# Revit family: oventrop_regudis-w-ht-duo_1341372rfa
name_source: partatom
category: Оборудование
revit_build: Autodesk Revit 2017 (Build: 20160225_1515(x64)
units: mm (PartAtom-declared; Revit-internal decimal feet)

## family parameters
Всегда вертикально = Да
Заголовок OmniClass = Climate Control (HVAC)
На основе рабочей плоскости = Нет
Номер OmniClass = 23.75.00.00
Общий = Нет
При загрузке вырезать с полостями = Нет
Размер круглого соединителя = Использовать диаметр
Тип детали = Нормальный
Точка расчета площади = Нет

## types (1)
- 17 l/min
    Article Description = Dwelling station, hot potable water performance range - 17 l/min
    Article Type = 17 l/min
    Connection Diameter = 19 мм
    Connection Set Length = 31 мм
    Custom = Нет
    Depth = 150 мм
    EMCS Version = 2.0
    ETIM Article Class = EC000431
    Family Version = 10.15
    GTIN = 4026755430974
    Grey = Color RGB 140-140-140
    Height = 645 мм
    IFCExportAs = IfcHeatExchangerType
    IFCExportType = NOTDEFINED
    Length = 630 мм
    MEPcontent Class = HEAT_EXCHANGER
    Manufacturer Art. No. = 1341372
    Manufacturer URL = http://www.oventrop.com
    Power = 42000 В·А
    Primary Volume Flow = 0.0 л/с
    Product Line = Oventrop
    Revit Version = 2015
    Secondary Volume Flow = 0.0 л/с
    URL = http://file-system.ru
    Use Nominal Diameter = Да
    Voltage = 230 В
    White = Color RAL 9010
    Yellow = Color RGB 168-128-048
    Группа модели = 17 l/min
    Изготовитель = Oventrop
    Описание = Dwelling station, hot potable water performance range - 17 l/min

## geometry (parser evidence)
native form markers: Sweep x2
no freeform markers — native parametric forms only
